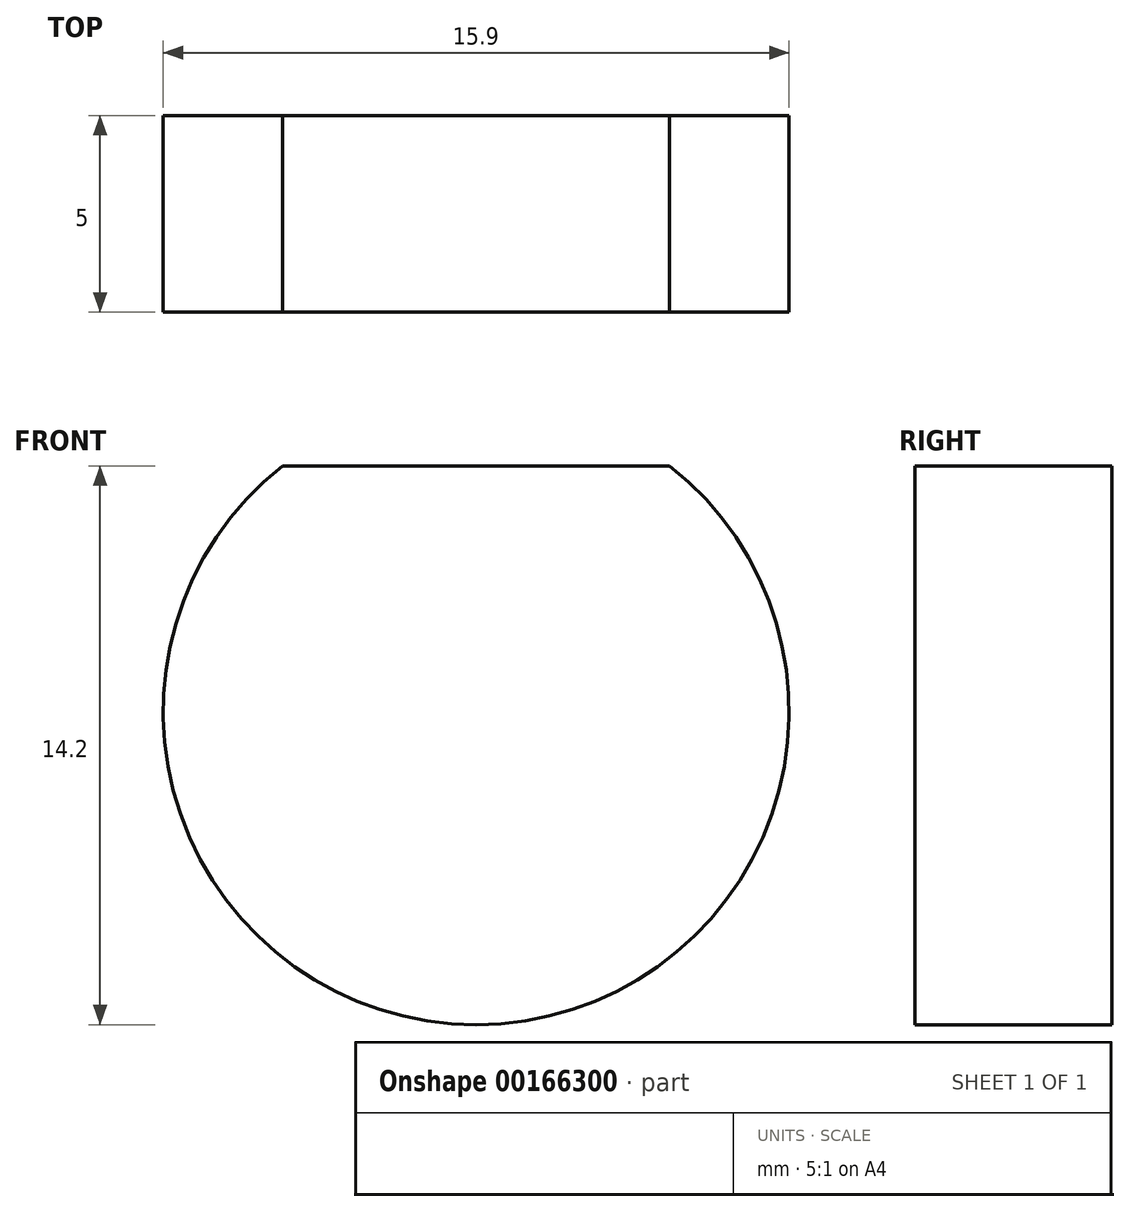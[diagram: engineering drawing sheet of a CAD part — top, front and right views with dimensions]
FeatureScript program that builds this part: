
annotation { "Feature Type Name" : "Feature", "Feature Type Description" : "" }
export const myFeature = defineFeature(function(context is Context, id is Id, definition is map)
    precondition{}
    {
        {
            assignVariable(context, id + "F0", {"name" : "Main_Length", "anyValue" : 5});
        }
        {
            var Q0;
            Q0=qCreatedBy(makeId("Front.planeOp"),FACE);
            var sketch = newSketch(context, id + "F1", { "sketchPlane" : qUnion([Q0])});
            skArc(sketch, "E0", {"start": v(-4.91, 6.25) * mm, "mid": v(0, -7.95) * mm, "end": v(4.91, 6.25) * mm});
            skLineSegment(sketch, "E1", {"start": v(-4.91, 6.25) * mm, "end": v(4.91, 6.25) * mm});
            skSolve(sketch);
        }
        {
            var Q0;
            Q0=makeQuery(id+"F1.imprint","IMPRINT",FACE,{"disambiguationData":[TD([[makeQuery(id+"F1.imprint","IMPRINT",EDGE,{"derivedFrom":sQuery(id+"F1.wireOp",EDGE,"E0")}),1.0]])]});
            extrude(context, id + "F2", {"entities" : qUnion([Q0]), "depth" : (getVariable(context, 'Main_Length')) * mm});
        }
    });
